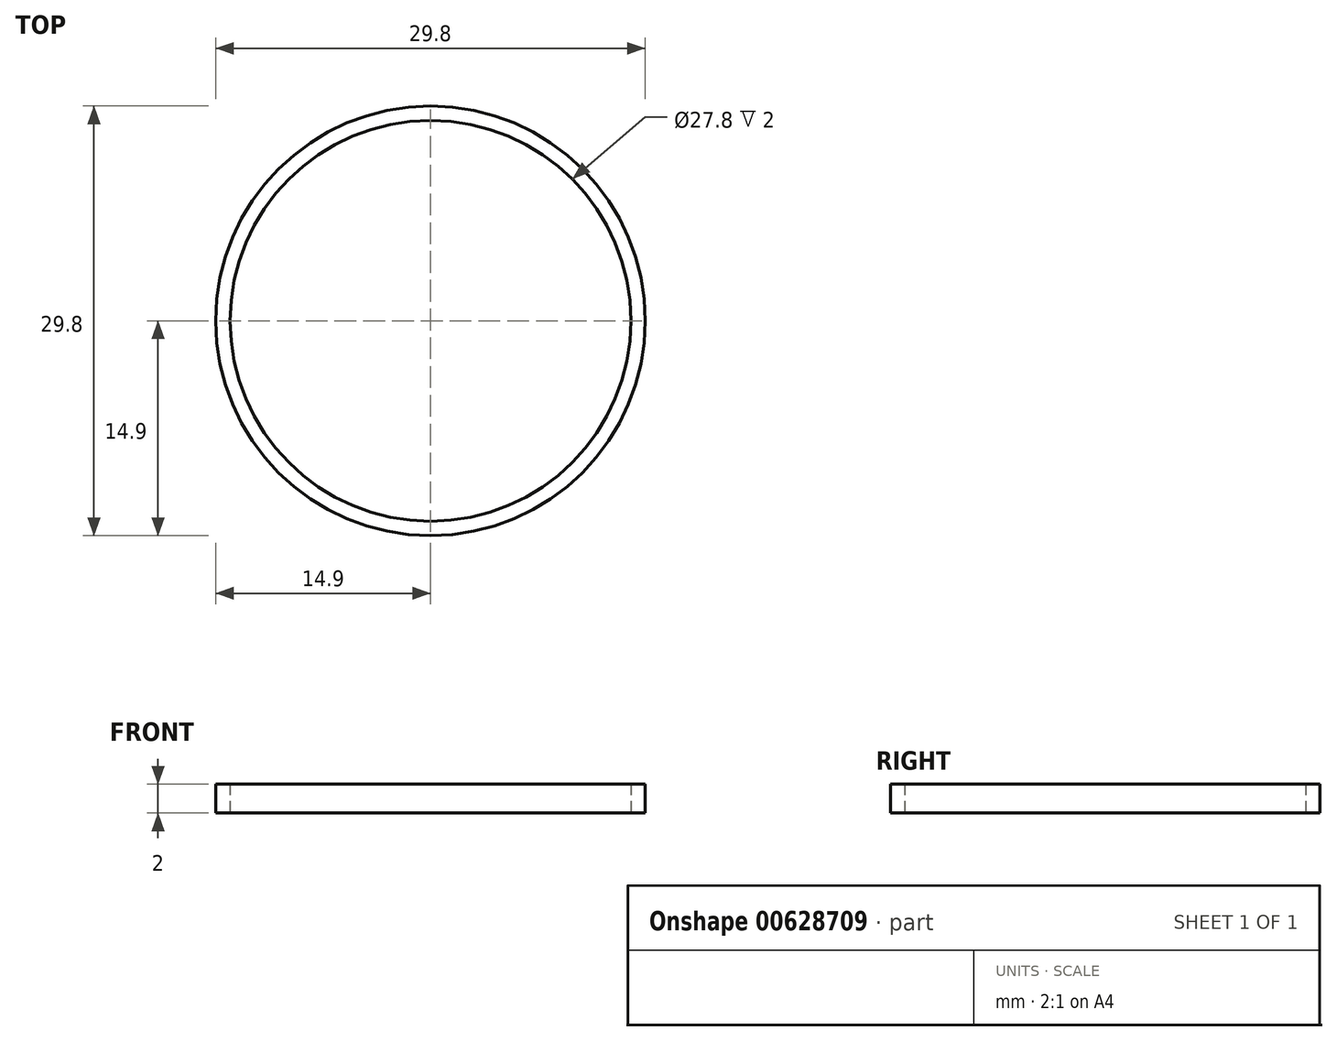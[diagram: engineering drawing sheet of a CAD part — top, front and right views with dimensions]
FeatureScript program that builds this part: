
annotation { "Feature Type Name" : "Feature", "Feature Type Description" : "" }
export const myFeature = defineFeature(function(context is Context, id is Id, definition is map)
    precondition{}
    {
        {
            var Q0;
            Q0=qCreatedBy(makeId("Top.planeOp"),FACE);
            var sketch = newSketch(context, id + "F0", { "sketchPlane" : qUnion([Q0])});
            skCircle(sketch, "E0", {"center": v(0, 0) * mm, "radius": 14.9 * mm});
            skCircle(sketch, "E1", {"center": v(0, 0) * mm, "radius": 13.9 * mm});
            skSolve(sketch);
        }
        {
            var Q0;
            Q0 = qSketchRegion(id + "F0", true);
            extrude(context, id + "F1", {"entities" : qUnion([Q0]), "endBound" : BoundingType.SYMMETRIC, "depth" : 2 * mm, "offsetDistance" : 25 * mm});
        }
    });
